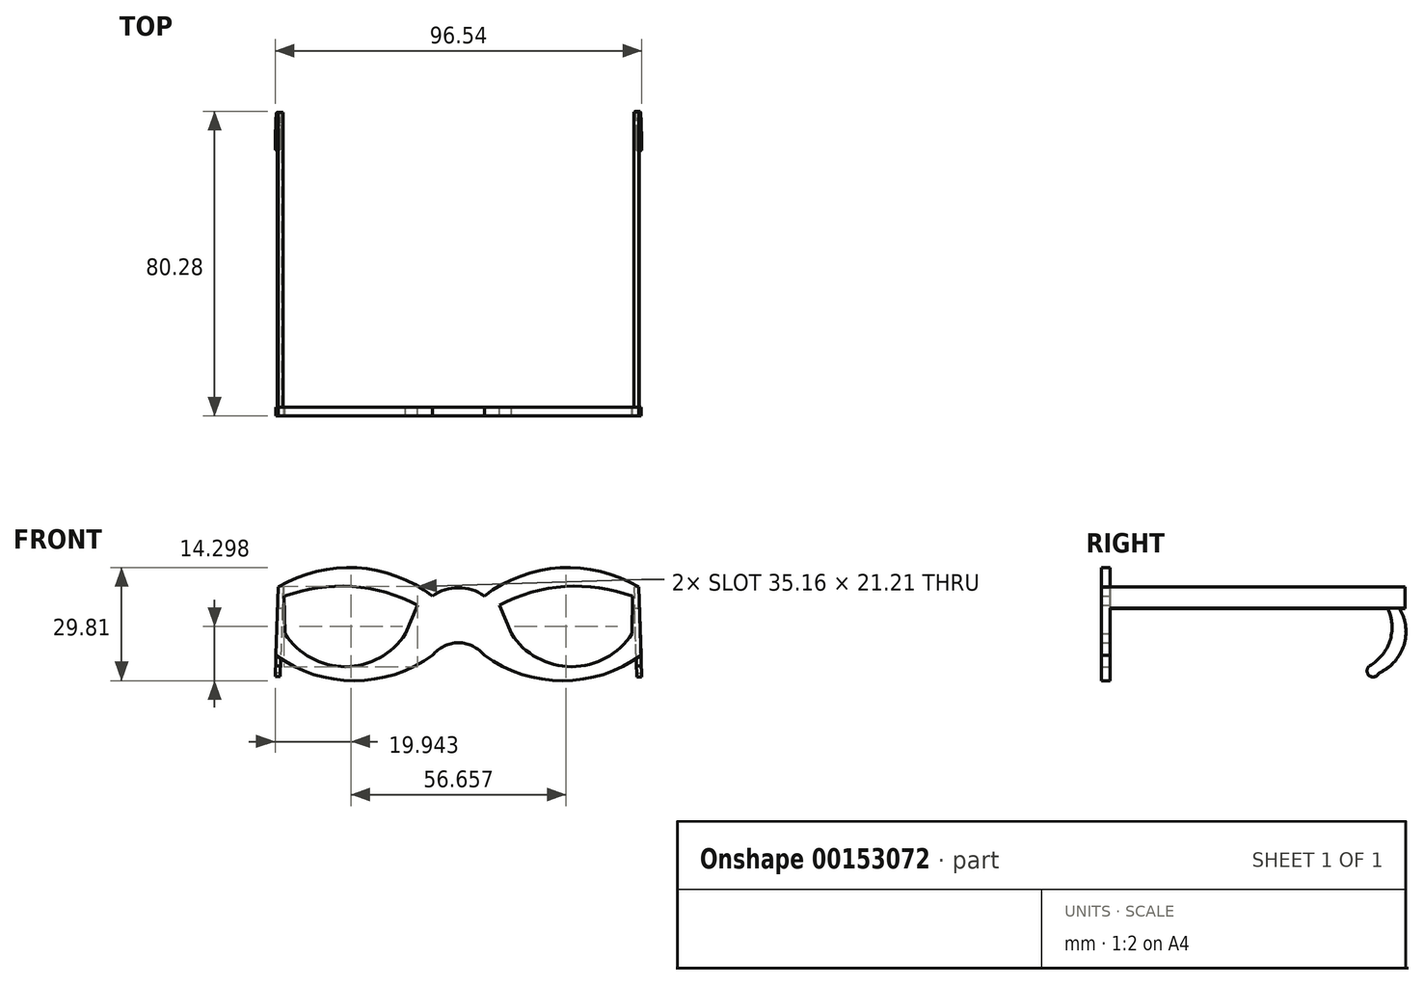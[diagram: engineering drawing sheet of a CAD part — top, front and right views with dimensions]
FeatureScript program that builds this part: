
annotation { "Feature Type Name" : "Feature", "Feature Type Description" : "" }
export const myFeature = defineFeature(function(context is Context, id is Id, definition is map)
    precondition{}
    {
        {
            var Q0;
            Q0=qCreatedBy(makeId("Front.planeOp"),FACE);
            var sketch = newSketch(context, id + "F0", { "sketchPlane" : qUnion([Q0])});
            skPoint(sketch, "E0.visualSharp", {"position": v(-4.72, 17.48) * mm});
            skPoint(sketch, "E1.visualSharp", {"position": v(-4.72, -13.38) * mm});
            skArc(sketch, "E2", {"start": v(8.9, 9.86) * mm, "mid": v(2.1, 12.07) * mm, "end": v(-4.72, 9.86) * mm});
            skArc(sketch, "E3", {"start": v(8.9, -5.76) * mm, "mid": v(2.1, -2.46) * mm, "end": v(-4.72, -5.76) * mm});
            skArc(sketch, "E4", {"start": v(-4.72, 9.86) * mm, "mid": v(-24.7, 17.3) * mm, "end": v(-45.41, 12.25) * mm});
            skArc(sketch, "E5", {"start": v(-46, -5.76) * mm, "mid": v(-25.36, -12.45) * mm, "end": v(-4.72, -5.76) * mm});
            skArc(sketch, "E6", {"start": v(-8.66, 7.43) * mm, "mid": v(-25.98, 12.39) * mm, "end": v(-43.82, 9.82) * mm});
            skArc(sketch, "E7", {"start": v(-43.63, 0) * mm, "mid": v(-27.73, -8.76) * mm, "end": v(-11.84, 0) * mm});
            skLineSegment(sketch, "E8", {"start": v(-43.82, 9.82) * mm, "end": v(-43.63, 0) * mm});
            skLineSegment(sketch, "E9", {"start": v(-11.84, 0) * mm, "end": v(-8.66, 7.43) * mm});
            skArc(sketch, "E10.MirrorCS", {"start": v(50.18, -5.76) * mm, "mid": v(29.54, -12.45) * mm, "end": v(8.9, -5.76) * mm});
            skPoint(sketch, "E11.MirrorP", {"position": v(8.9, 17.48) * mm});
            skArc(sketch, "E12.MirrorCS", {"start": v(47.81, 0) * mm, "mid": v(31.92, -8.76) * mm, "end": v(16.02, 0) * mm});
            skLineSegment(sketch, "E13.MirrorCS", {"start": v(48, 9.82) * mm, "end": v(47.81, 0) * mm});
            skArc(sketch, "E14.MirrorCS", {"start": v(12.84, 7.43) * mm, "mid": v(30.17, 12.39) * mm, "end": v(48, 9.82) * mm});
            skLineSegment(sketch, "E15.MirrorCS", {"start": v(16.02, 0) * mm, "end": v(12.84, 7.43) * mm});
            skArc(sketch, "E16.MirrorCS", {"start": v(8.9, 9.86) * mm, "mid": v(28.88, 17.3) * mm, "end": v(49.6, 12.25) * mm});
            skPoint(sketch, "E17.MirrorP", {"position": v(8.9, -13.38) * mm});
            skLineSegment(sketch, "E18", {"start": v(49.6, 12.25) * mm, "end": v(50.18, -5.76) * mm});
            skLineSegment(sketch, "E19", {"start": v(-45.41, 12.25) * mm, "end": v(-46, -5.76) * mm});
            skSolve(sketch);
        }
        {
            var Q0;
            Q0=makeQuery(id+"F0.imprint","IMPRINT",FACE,{"disambiguationData":[TD([[makeQuery(id+"F0.imprint","IMPRINT",EDGE,{"derivedFrom":sQuery(id+"F0.wireOp",EDGE,"E2")}),1.0]])]});
            extrude(context, id + "F1", {"entities" : qUnion([Q0]), "depth" : 2.3 * mm});
        }
        {
            var Q0;
            Q0=makeQuery(id+"F1.opExtrude","SWEPT_FACE",FACE,{"disambiguationData":[OSD([sQuery(id+"F0.wireOp",EDGE,"E19")])]});
            var sketch = newSketch(context, id + "F2", { "sketchPlane" : qUnion([Q0])});
            skLineSegment(sketch, "E20.bottom", {"start": v(0, 10.78) * mm, "end": v(-77.76, 10.78) * mm});
            skLineSegment(sketch, "E20.top", {"start": v(0, 5.08) * mm, "end": v(-77.76, 5.08) * mm});
            skLineSegment(sketch, "E20.left", {"start": v(0, 10.78) * mm, "end": v(0, 5.08) * mm});
            skLineSegment(sketch, "E20.right", {"start": v(-77.76, 10.78) * mm, "end": v(-77.76, 5.08) * mm});
            skSolve(sketch);
        }
        {
            var Q0;
            Q0=makeQuery(id+"F2.imprint","IMPRINT",FACE,{"disambiguationData":[TD([[makeQuery(id+"F2.imprint","IMPRINT",EDGE,{"derivedFrom":sQuery(id+"F2.wireOp",EDGE,"E20.bottom")}),1.0]])]});
            extrude(context, id + "F3", {"entities" : qUnion([Q0]), "operationType" : NewBodyOperationType.ADD, "oppositeDirection" : true, "depth" : 1.27 * mm});
        }
        {
            var Q0;
            Q0=makeQuery(id+"F1.opExtrude","SWEPT_FACE",FACE,{"disambiguationData":[OSD([sQuery(id+"F0.wireOp",EDGE,"E18")])]});
            var sketch = newSketch(context, id + "F4", { "sketchPlane" : qUnion([Q0])});
            skLineSegment(sketch, "E21.bottom", {"start": v(0, 10.64) * mm, "end": v(77.81, 10.64) * mm});
            skLineSegment(sketch, "E21.top", {"start": v(0, 5.07) * mm, "end": v(77.81, 5.07) * mm});
            skLineSegment(sketch, "E21.left", {"start": v(0, 10.64) * mm, "end": v(0, 5.07) * mm});
            skLineSegment(sketch, "E21.right", {"start": v(77.81, 10.64) * mm, "end": v(77.81, 5.07) * mm});
            skSolve(sketch);
        }
        {
            var Q0;
            Q0=makeQuery(id+"F4.imprint","IMPRINT",FACE,{"disambiguationData":[TD([[makeQuery(id+"F4.imprint","IMPRINT",EDGE,{"derivedFrom":sQuery(id+"F4.wireOp",EDGE,"E21.bottom")}),-1.0]])]});
            extrude(context, id + "F5", {"entities" : qUnion([Q0]), "operationType" : NewBodyOperationType.ADD, "oppositeDirection" : true, "depth" : 1.27 * mm});
        }
        {
            var Q0;
            Q0=makeQuery(id+"F3.opExtrude","SWEPT_FACE",FACE,{"disambiguationData":[OSD([sQuery(id+"F2.wireOp",EDGE,"E20.bottom")])]});
            var sketch = newSketch(context, id + "F6", { "sketchPlane" : qUnion([Q0])});
            skArc(sketch, "E22", {"start": v(-6.03, 117.24) * mm, "mid": v(-36.76, 108.43) * mm, "end": v(-45.79, 77.76) * mm});
            skArc(sketch, "E23", {"start": v(-6.65, 114.6) * mm, "mid": v(-35.88, 106.76) * mm, "end": v(-44.52, 77.76) * mm});
            skSolve(sketch);
        }
        {
            var Q0;
            Q0=makeQuery(id+"F5.opExtrude","SWEPT_FACE",FACE,{"disambiguationData":[OSD([sQuery(id+"F4.wireOp",EDGE,"E21.bottom")])]});
            var sketch = newSketch(context, id + "F7", { "sketchPlane" : qUnion([Q0])});
            skArc(sketch, "E24", {"start": v(49.97, 77.81) * mm, "mid": v(30.66, 109.23) * mm, "end": v(-5.33, 117.24) * mm});
            skArc(sketch, "E25", {"start": v(48.7, 77.81) * mm, "mid": v(29.05, 107.7) * mm, "end": v(-6, 114.86) * mm});
            skSolve(sketch);
        }
        {
            var Q0;
            Q0=sQuery(id+"F7.wireOp",EDGE,"E24");
            var Q1;
            Q1=sQuery(id+"F7.wireOp",EDGE,"E25");
            var Q2;
            Q2=sQuery(id+"F6.wireOp",EDGE,"E22");
            var Q3;
            Q3=sQuery(id+"F6.wireOp",EDGE,"E23");
            extrude(context, id + "F8", {"bodyType" : ToolBodyType.SURFACE, "surfaceEntities" : qUnion([Q0, Q1, Q2, Q3]), "oppositeDirection" : true, "depth" : 5.84 * mm});
        }
        {
            var Q0;
            Q0=makeQuery(id+"F5.boolean.opBoolean","MERGE",FACE,{"derivedFrom":[makeQuery(id+"F1.opExtrude","SWEPT_FACE",FACE,{"disambiguationData":[OSD([sQuery(id+"F0.wireOp",EDGE,"E18")])]}),makeQuery(id+"F5.opExtrude","CAP_FACE",FACE,{"disambiguationData":[OSD([sQuery(id+"F4.wireOp",EDGE,"E21.bottom"),sQuery(id+"F4.wireOp",EDGE,"E21.top"),sQuery(id+"F4.wireOp",EDGE,"E21.left"),sQuery(id+"F4.wireOp",EDGE,"E21.right")])],"isStart":true})]});
            var sketch = newSketch(context, id + "F9", { "sketchPlane" : qUnion([Q0])});
            skArc(sketch, "E26", {"start": v(70.87, -12.03) * mm, "mid": v(77.44, -4.7) * mm, "end": v(76.25, 5.07) * mm});
            skArc(sketch, "E27", {"start": v(68.41, -10.16) * mm, "mid": v(73.8, -3.49) * mm, "end": v(73.2, 5.07) * mm});
            skArc(sketch, "E28", {"start": v(68.41, -10.16) * mm, "mid": v(68.38, -12.74) * mm, "end": v(70.87, -12.03) * mm});
            skSolve(sketch);
        }
        {
            var Q0;
            Q0=makeQuery(id+"F3.boolean.opBoolean","MERGE",FACE,{"derivedFrom":[makeQuery(id+"F1.opExtrude","SWEPT_FACE",FACE,{"disambiguationData":[OSD([sQuery(id+"F0.wireOp",EDGE,"E19")])]}),makeQuery(id+"F3.opExtrude","CAP_FACE",FACE,{"disambiguationData":[OSD([sQuery(id+"F2.wireOp",EDGE,"E20.bottom"),sQuery(id+"F2.wireOp",EDGE,"E20.top"),sQuery(id+"F2.wireOp",EDGE,"E20.left"),sQuery(id+"F2.wireOp",EDGE,"E20.right")])],"isStart":true})]});
            var sketch = newSketch(context, id + "F10", { "sketchPlane" : qUnion([Q0])});
            skArc(sketch, "E29", {"start": v(-73.2, 5.08) * mm, "mid": v(-73.78, -3.41) * mm, "end": v(-68.41, -10.02) * mm});
            skArc(sketch, "E30", {"start": v(-76.13, 5.08) * mm, "mid": v(-77.17, -4.54) * mm, "end": v(-70.87, -11.9) * mm});
            skArc(sketch, "E31", {"start": v(-70.87, -11.9) * mm, "mid": v(-68.47, -12.5) * mm, "end": v(-68.41, -10.02) * mm});
            skSolve(sketch);
        }
        {
            var Q0;
            {var subQ0=sQuery(id+"F10.wireOp",EDGE,"E29");Q0=makeQuery(id+"F10.imprint","IMPRINT",FACE,{"disambiguationData":[TD([[makeQuery(id+"F10.imprint","IMPRINT",EDGE,{"derivedFrom":subQ0}),-1.0]])]});}
            extrude(context, id + "F11", {"entities" : qUnion([Q0]), "operationType" : NewBodyOperationType.ADD, "oppositeDirection" : true, "depth" : 1.27 * mm});
        }
        {
            var Q0;
            {var subQ0=sQuery(id+"F9.wireOp",EDGE,"E26");Q0=makeQuery(id+"F9.imprint","IMPRINT",FACE,{"disambiguationData":[TD([[makeQuery(id+"F9.imprint","IMPRINT",EDGE,{"derivedFrom":subQ0}),1.0]])]});}
            extrude(context, id + "F12", {"entities" : qUnion([Q0]), "oppositeDirection" : true, "depth" : 1.27 * mm});
        }
    });
